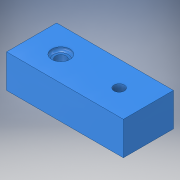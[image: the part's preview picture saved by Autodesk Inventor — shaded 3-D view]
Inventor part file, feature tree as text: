
AUTODESK INVENTOR PART (.ipt)
format: ipt  version: 2018 (Build 220112000, 112)  size: 126,976 bytes
history: native  units: in
note: dims shown in document units (in); Inventor stores cm internally (conversion verified against a paired STEP export)
features: sketch x2, extrude x1, revolve x1, projected_geometry x1
ambient origin geometry x8: Origin, YZ Plane, XZ Plane, XY Plane, X Axis, Y Axis, Z Axis, Center Point
bodies: Body1 (feature_tree)
feature tree (5):
  extrude  "Extrusion5"  Depth=3.5in
  revolve  "Revolution1"  [1 undecoded]
  sketch  "Sketch1"  dims[d3=1.5in d4=3.5in]
  sketch  "Sketch8"  dims[d20=0.3125in d21=1.0in d22=0.875in d23=0.875in d24=1.0in d25=0.0in d34=0.139in d35=0.05in d36=90.0deg]
  projected_geometry  "Projected Loop5"
note: 1 required parameter value undecoded (feature->parameter linkage not recoverable at this tier; creation-order binding heuristic only, values carry confidence <= 0.55)
